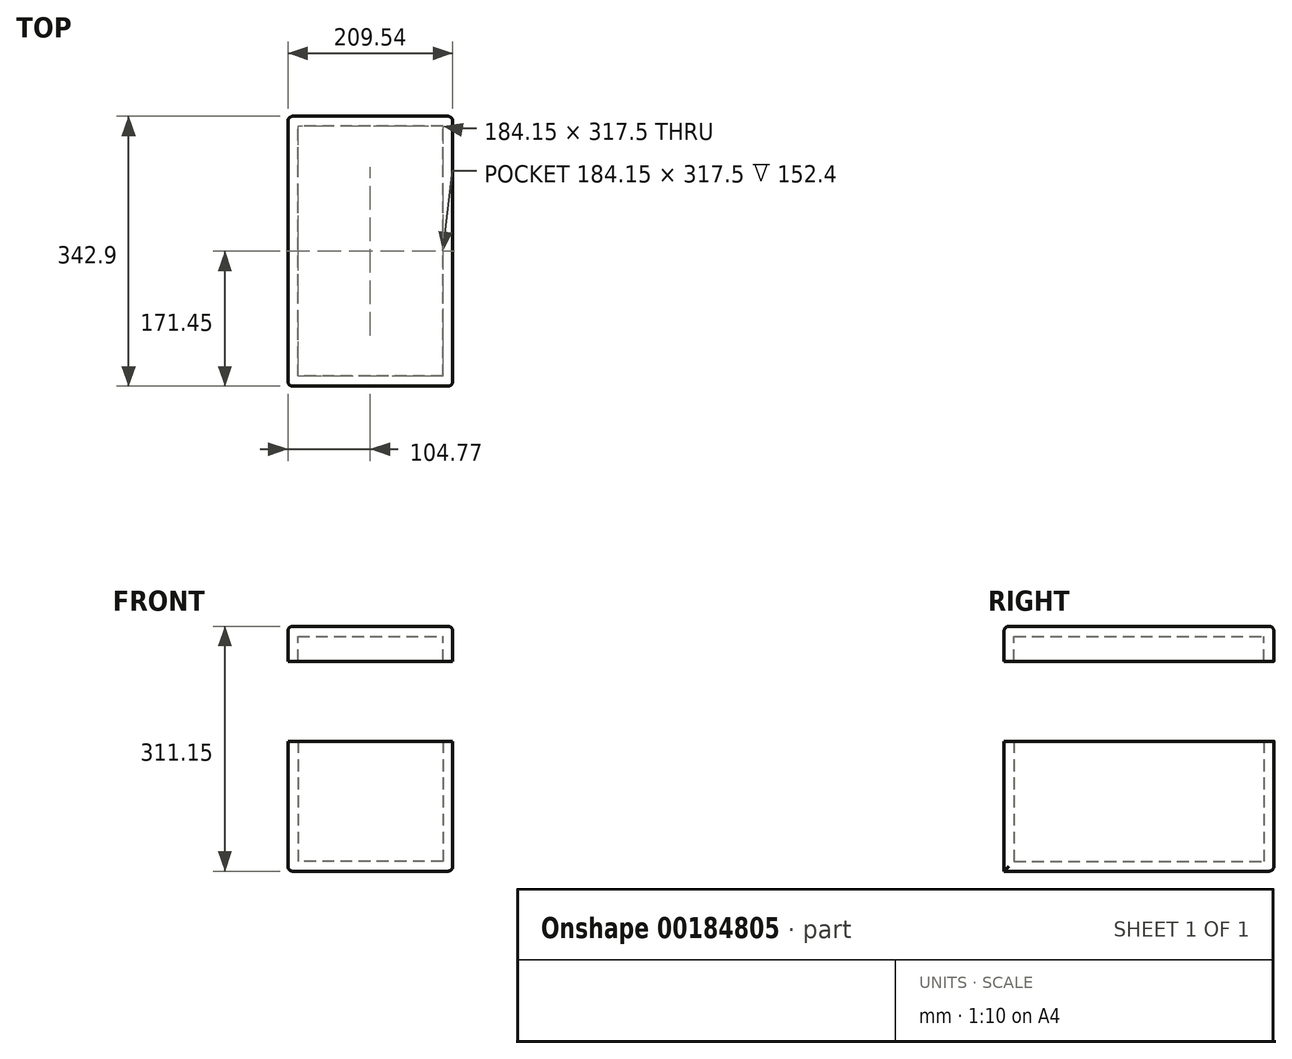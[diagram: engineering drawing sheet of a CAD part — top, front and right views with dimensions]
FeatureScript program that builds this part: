
annotation { "Feature Type Name" : "Feature", "Feature Type Description" : "" }
export const myFeature = defineFeature(function(context is Context, id is Id, definition is map)
    precondition{}
    {
        {
            var Q0;
            Q0=qCreatedBy(makeId("Front.planeOp"),FACE);
            var sketch = newSketch(context, id + "F0", { "sketchPlane" : qUnion([Q0])});
            skLineSegment(sketch, "E0.bottom", {"start": v(104.77, 82.55) * mm, "end": v(-104.78, 82.55) * mm});
            skLineSegment(sketch, "E0.top", {"start": v(104.78, -82.55) * mm, "end": v(-104.77, -82.55) * mm});
            skLineSegment(sketch, "E0.left", {"start": v(104.77, 82.55) * mm, "end": v(104.78, -82.55) * mm});
            skLineSegment(sketch, "E0.right", {"start": v(-104.78, 82.55) * mm, "end": v(-104.77, -82.55) * mm});
            skPoint(sketch, "E0.middle", {"position": v(0, 0) * mm});
            skLineSegment(sketch, "E1.bottom", {"start": v(-104.78, 184.15) * mm, "end": v(104.77, 184.15) * mm});
            skLineSegment(sketch, "E1.top", {"start": v(-104.78, 228.6) * mm, "end": v(104.77, 228.6) * mm});
            skLineSegment(sketch, "E1.left", {"start": v(-104.78, 184.15) * mm, "end": v(-104.78, 228.6) * mm});
            skLineSegment(sketch, "E1.right", {"start": v(104.77, 184.15) * mm, "end": v(104.77, 228.6) * mm});
            skSolve(sketch);
        }
        {
            var Q0;
            Q0=makeQuery(id+"F0.imprint","IMPRINT",FACE,{"disambiguationData":[TD([[makeQuery(id+"F0.imprint","IMPRINT",EDGE,{"derivedFrom":sQuery(id+"F0.wireOp",EDGE,"E1.bottom")}),1.0]])]});
            var Q1;
            Q1=makeQuery(id+"F0.imprint","IMPRINT",FACE,{"disambiguationData":[TD([[makeQuery(id+"F0.imprint","IMPRINT",EDGE,{"derivedFrom":sQuery(id+"F0.wireOp",EDGE,"E0.bottom")}),1.0]])]});
            extrude(context, id + "F1", {"entities" : qUnion([Q0, Q1]), "depth" : 342.9 * mm, "offsetDistance" : 25.4 * mm});
        }
        {
            var Q0;
            Q0=makeQuery(id+"F1.opExtrude","SWEPT_FACE",FACE,{"disambiguationData":[OSD([sQuery(id+"F0.wireOp",EDGE,"E0.bottom")])]});
            var Q1;
            Q1=makeQuery(id+"F1.opExtrude","SWEPT_FACE",FACE,{"disambiguationData":[OSD([sQuery(id+"F0.wireOp",EDGE,"E1.bottom")])]});
            shell(context, id + "F2", {"entities" : qUnion([Q0, Q1]), "thickness" : 12.7 * mm});
        }
        {
            var Q0;
            Q0=makeQuery(id+"F1.opExtrude","CAP_EDGE",EDGE,{"disambiguationData":[OSD([sQuery(id+"F0.wireOp",EDGE,"E1.right")])],"isStart":false});
            var Q1;
            Q1=makeQuery(id+"F1.opExtrude","CAP_EDGE",EDGE,{"disambiguationData":[OSD([sQuery(id+"F0.wireOp",EDGE,"E0.left")])],"isStart":false});
            var Q2;
            Q2=makeQuery(id+"F1.opExtrude","CAP_EDGE",EDGE,{"disambiguationData":[OSD([sQuery(id+"F0.wireOp",EDGE,"E0.right")])],"isStart":false});
            var Q3;
            Q3=makeQuery(id+"F1.opExtrude","SWEPT_EDGE",EDGE,{"disambiguationData":[OSD([sQuery(id+"F0.wireOp",EDGE,"E0.top"),sQuery(id+"F0.wireOp",EDGE,"E0.left")])]});
            var Q4;
            Q4=makeQuery(id+"F1.opExtrude","CAP_EDGE",EDGE,{"disambiguationData":[OSD([sQuery(id+"F0.wireOp",EDGE,"E0.left")])],"isStart":true});
            var Q5;
            Q5=makeQuery(id+"F1.opExtrude","CAP_EDGE",EDGE,{"disambiguationData":[OSD([sQuery(id+"F0.wireOp",EDGE,"E1.right")])],"isStart":true});
            var Q6;
            Q6=makeQuery(id+"F1.opExtrude","SWEPT_EDGE",EDGE,{"disambiguationData":[OSD([sQuery(id+"F0.wireOp",EDGE,"E1.top"),sQuery(id+"F0.wireOp",EDGE,"E1.right")])]});
            var Q7;
            Q7=makeQuery(id+"F1.opExtrude","CAP_EDGE",EDGE,{"disambiguationData":[OSD([sQuery(id+"F0.wireOp",EDGE,"E1.top")])],"isStart":true});
            var Q8;
            Q8=makeQuery(id+"F1.opExtrude","SWEPT_EDGE",EDGE,{"disambiguationData":[OSD([sQuery(id+"F0.wireOp",EDGE,"E1.top"),sQuery(id+"F0.wireOp",EDGE,"E1.left")])]});
            var Q9;
            Q9=makeQuery(id+"F1.opExtrude","CAP_EDGE",EDGE,{"disambiguationData":[OSD([sQuery(id+"F0.wireOp",EDGE,"E1.top")])],"isStart":false});
            var Q10;
            Q10=makeQuery(id+"F1.opExtrude","CAP_EDGE",EDGE,{"disambiguationData":[OSD([sQuery(id+"F0.wireOp",EDGE,"E1.left")])],"isStart":false});
            var Q11;
            Q11=makeQuery(id+"F1.opExtrude","CAP_EDGE",EDGE,{"disambiguationData":[OSD([sQuery(id+"F0.wireOp",EDGE,"E0.right")])],"isStart":true});
            var Q12;
            Q12=makeQuery(id+"F1.opExtrude","CAP_EDGE",EDGE,{"disambiguationData":[OSD([sQuery(id+"F0.wireOp",EDGE,"E0.top")])],"isStart":true});
            var Q13;
            Q13=makeQuery(id+"F1.opExtrude","SWEPT_EDGE",EDGE,{"disambiguationData":[OSD([sQuery(id+"F0.wireOp",EDGE,"E0.top"),sQuery(id+"F0.wireOp",EDGE,"E0.right")])]});
            var Q14;
            Q14=makeQuery(id+"F1.opExtrude","CAP_EDGE",EDGE,{"disambiguationData":[OSD([sQuery(id+"F0.wireOp",EDGE,"E1.left")])],"isStart":true});
            fillet(context, id + "F3", {"entities" : qUnion([Q0, Q1, Q2, Q3, Q4, Q5, Q6, Q7, Q8, Q9, Q10, Q11, Q12, Q13, Q14]), "tangentPropagation" : true, "radius" : 6.35 * mm, "defaultsChanged" : false, "vertexSettings" : [], "allowEdgeOverflow" : false});
        }
    });
